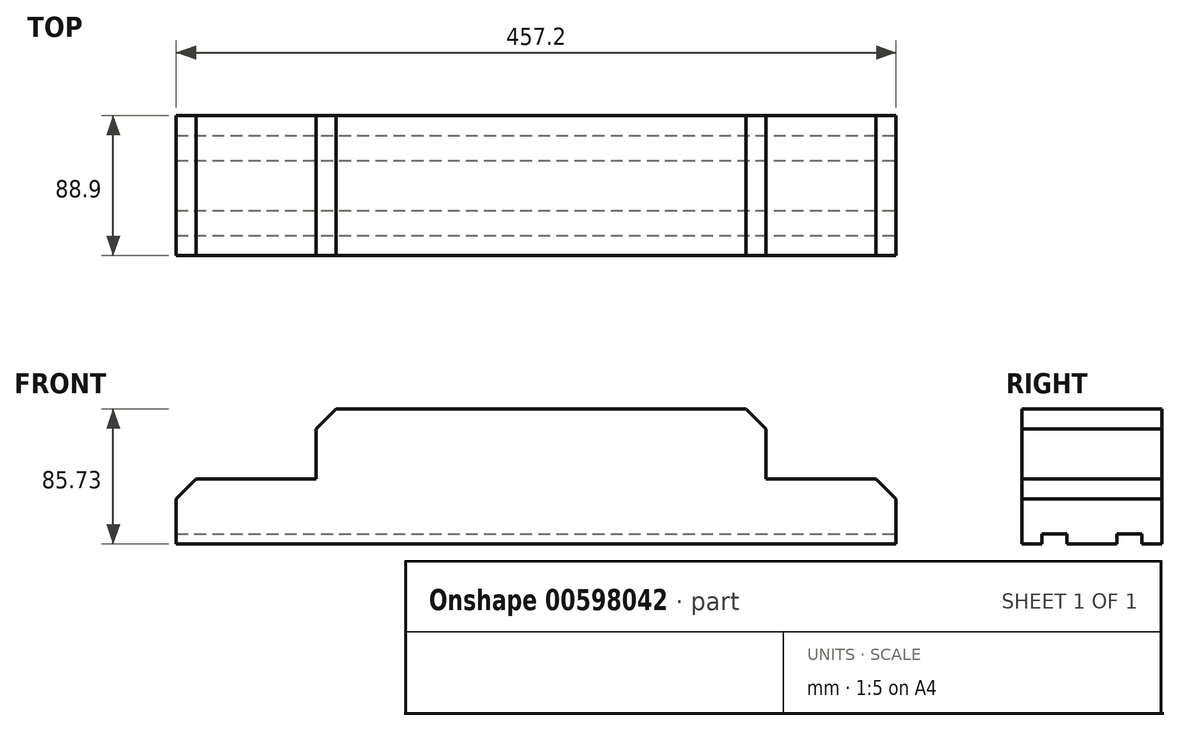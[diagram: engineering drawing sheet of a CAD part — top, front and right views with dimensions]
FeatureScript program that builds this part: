
annotation { "Feature Type Name" : "Feature", "Feature Type Description" : "" }
export const myFeature = defineFeature(function(context is Context, id is Id, definition is map)
    precondition{}
    {
        {
            var Q0;
            Q0=qCreatedBy(makeId("Front.planeOp"),FACE);
            var sketch = newSketch(context, id + "F0", { "sketchPlane" : qUnion([Q0])});
            skLineSegment(sketch, "E0.bottom", {"start": v(228.6, 20.64) * mm, "end": v(146.05, 20.64) * mm});
            skLineSegment(sketch, "E0.top", {"start": v(228.6, -20.64) * mm, "end": v(-228.6, -20.64) * mm});
            skLineSegment(sketch, "E0.left", {"start": v(228.6, 20.64) * mm, "end": v(228.6, -20.64) * mm});
            skLineSegment(sketch, "E0.right", {"start": v(-228.6, 20.64) * mm, "end": v(-228.6, -20.64) * mm});
            skPoint(sketch, "E0.middle", {"position": v(0, 0) * mm});
            skLineSegment(sketch, "E1", {"start": v(-139.7, 65.09) * mm, "end": v(-139.7, 20.64) * mm});
            skLineSegment(sketch, "E2", {"start": v(-139.7, 65.09) * mm, "end": v(146.05, 65.09) * mm});
            skLineSegment(sketch, "E3", {"start": v(146.05, 65.09) * mm, "end": v(146.05, 20.64) * mm});
            skLineSegment(sketch, "E4.trimOffspring", {"start": v(-139.7, 20.64) * mm, "end": v(-228.6, 20.64) * mm});
            skSolve(sketch);
        }
        {
            var Q0;
            Q0 = qSketchRegion(id + "F0", true);
            extrude(context, id + "F1", {"entities" : qUnion([Q0]), "endBound" : BoundingType.SYMMETRIC, "depth" : 88.9 * mm, "offsetDistance" : 25.4 * mm});
        }
        {
            var Q0;
            Q0=makeQuery(id+"F1.opExtrude","SWEPT_EDGE",EDGE,{"disambiguationData":[OSD([sQuery(id+"F0.wireOp",EDGE,"E2"),sQuery(id+"F0.wireOp",EDGE,"E3")])]});
            var Q1;
            Q1=makeQuery(id+"F1.opExtrude","SWEPT_EDGE",EDGE,{"disambiguationData":[OSD([sQuery(id+"F0.wireOp",EDGE,"E1"),sQuery(id+"F0.wireOp",EDGE,"E2")])]});
            var Q2;
            Q2=makeQuery(id+"F1.opExtrude","SWEPT_EDGE",EDGE,{"disambiguationData":[OSD([sQuery(id+"F0.wireOp",EDGE,"E0.right"),sQuery(id+"F0.wireOp",EDGE,"E4.trimOffspring")])]});
            var Q3;
            Q3=makeQuery(id+"F1.opExtrude","SWEPT_EDGE",EDGE,{"disambiguationData":[OSD([sQuery(id+"F0.wireOp",EDGE,"E0.bottom"),sQuery(id+"F0.wireOp",EDGE,"E0.left")])]});
            chamfer(context, id + "F2", {"entities" : qUnion([Q0, Q1, Q2, Q3]), "width" : 12.7 * mm, "tangentPropagation" : true});
        }
        {
            var Q0;
            Q0=qCreatedBy(makeId("Right.planeOp"),FACE);
            var sketch = newSketch(context, id + "F3", { "sketchPlane" : qUnion([Q0])});
            skPoint(sketch, "E5.middle", {"position": v(0, 0) * mm});
            skLineSegment(sketch, "E6", {"start": v(-31.75, -14.29) * mm, "end": v(-15.88, -14.29) * mm});
            skLineSegment(sketch, "E7", {"start": v(-15.88, -20.64) * mm, "end": v(-15.88, -14.29) * mm});
            skLineSegment(sketch, "E8", {"start": v(-31.75, -14.29) * mm, "end": v(-31.75, -20.64) * mm});
            skLineSegment(sketch, "E9", {"start": v(31.75, -20.64) * mm, "end": v(31.75, -14.29) * mm});
            skLineSegment(sketch, "E10", {"start": v(31.75, -14.29) * mm, "end": v(15.88, -14.29) * mm});
            skLineSegment(sketch, "E11", {"start": v(15.88, -14.29) * mm, "end": v(15.88, -20.64) * mm});
            skLineSegment(sketch, "E12", {"start": v(-31.75, -20.64) * mm, "end": v(-15.88, -20.64) * mm});
            skLineSegment(sketch, "E13", {"start": v(15.88, -20.64) * mm, "end": v(31.75, -20.64) * mm});
            skSolve(sketch);
        }
        {
            var Q0;
            Q0 = qSketchRegion(id + "F3", true);
            extrude(context, id + "F4", {"entities" : qUnion([Q0]), "operationType" : NewBodyOperationType.REMOVE, "endBound" : BoundingType.SYMMETRIC, "oppositeDirection" : true, "depth" : 482.6 * mm, "offsetDistance" : 25.4 * mm});
        }
    });
